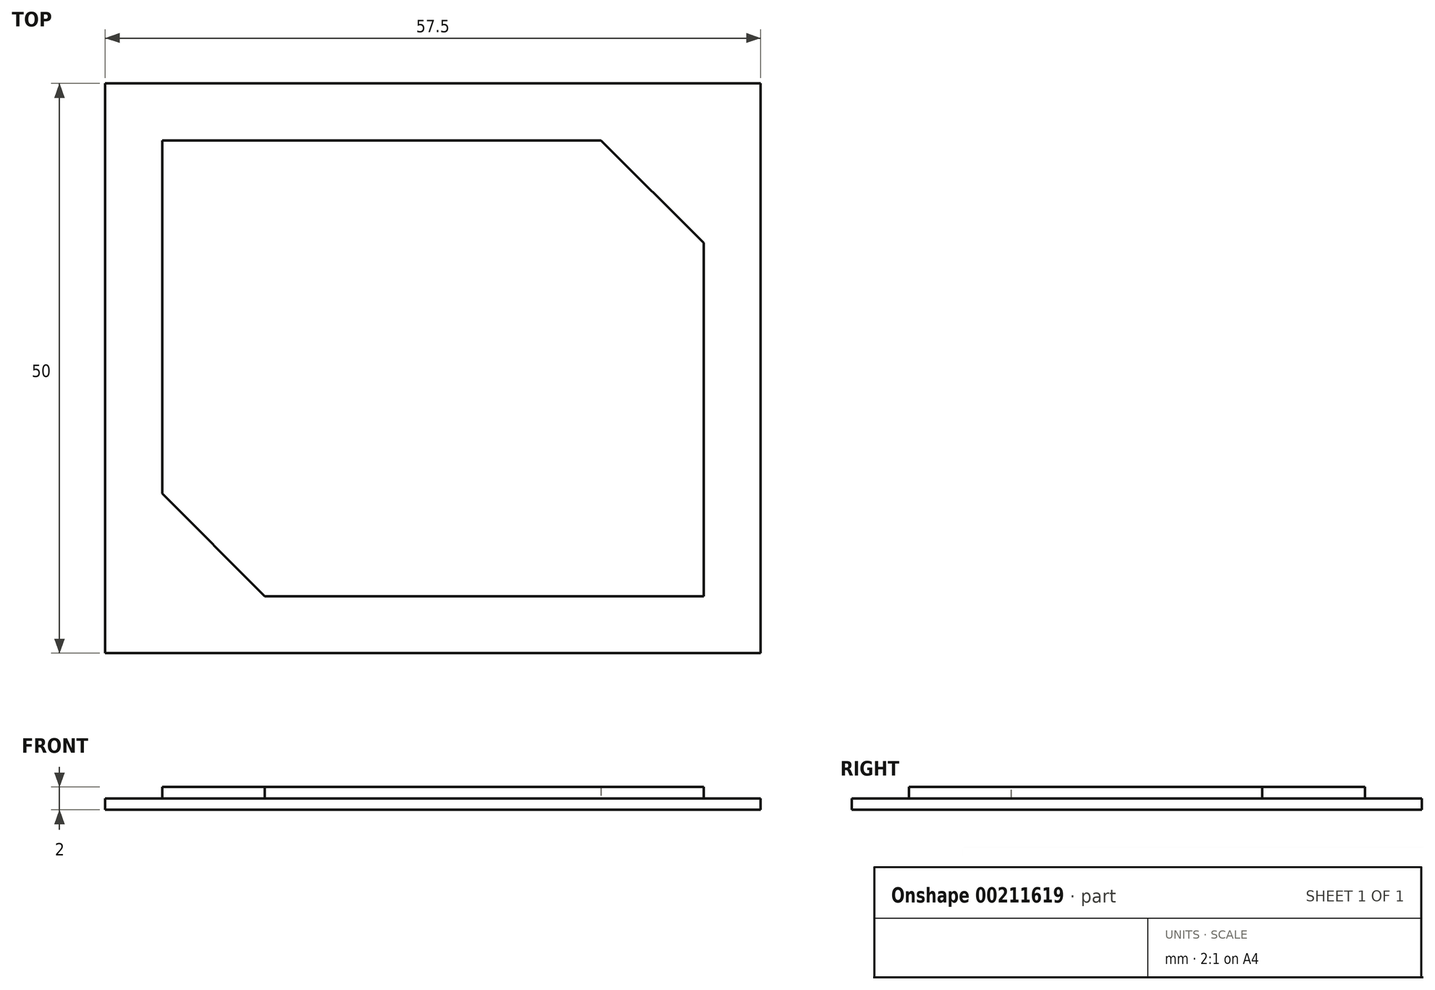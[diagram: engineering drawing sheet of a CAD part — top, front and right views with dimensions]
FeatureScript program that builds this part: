
annotation { "Feature Type Name" : "Feature", "Feature Type Description" : "" }
export const myFeature = defineFeature(function(context is Context, id is Id, definition is map)
    precondition{}
    {
        {
            var Q0;
            Q0=qCreatedBy(makeId("Top.planeOp"),FACE);
            var sketch = newSketch(context, id + "F0", { "sketchPlane" : qUnion([Q0])});
            skLineSegment(sketch, "E0.bottom", {"start": v(23.75, -20) * mm, "end": v(-23.75, -20) * mm});
            skLineSegment(sketch, "E0.top", {"start": v(23.75, 20) * mm, "end": v(-23.75, 20) * mm});
            skLineSegment(sketch, "E0.left", {"start": v(23.75, -20) * mm, "end": v(23.75, 20) * mm});
            skLineSegment(sketch, "E0.right", {"start": v(-23.75, -20) * mm, "end": v(-23.75, 20) * mm});
            skPoint(sketch, "E0.middle", {"position": v(0, 0) * mm});
            skLineSegment(sketch, "E1.0", {"start": v(28.75, -25) * mm, "end": v(-28.75, -25) * mm});
            skLineSegment(sketch, "E1.1", {"start": v(28.75, -25) * mm, "end": v(28.75, 25) * mm});
            skLineSegment(sketch, "E1.2", {"start": v(28.75, 25) * mm, "end": v(-28.75, 25) * mm});
            skLineSegment(sketch, "E1.3", {"start": v(-28.75, -25) * mm, "end": v(-28.75, 25) * mm});
            skSolve(sketch);
        }
        {
            var Q0;
            Q0=makeQuery(id+"F0.imprint","IMPRINT",FACE,{"disambiguationData":[TD([[makeQuery(id+"F0.imprint","IMPRINT",EDGE,{"derivedFrom":sQuery(id+"F0.wireOp",EDGE,"E0.bottom")}),-1.0]])]});
            extrude(context, id + "F1", {"entities" : qUnion([Q0]), "depth" : 2 * mm});
        }
        {
            var Q0;
            Q0=makeQuery(id+"F0.imprint","IMPRINT",FACE,{"disambiguationData":[TD([[makeQuery(id+"F0.imprint","IMPRINT",EDGE,{"derivedFrom":sQuery(id+"F0.wireOp",EDGE,"E0.bottom")}),1.0]])]});
            extrude(context, id + "F2", {"entities" : qUnion([Q0]), "operationType" : NewBodyOperationType.ADD, "depth" : 1 * mm});
        }
        {
            var Q0;
            Q0=makeQuery(id+"F1.opExtrude","SWEPT_EDGE",EDGE,{"disambiguationData":[OSD([sQuery(id+"F0.wireOp",EDGE,"E0.bottom"),sQuery(id+"F0.wireOp",EDGE,"E0.right")])]});
            var Q1;
            Q1=makeQuery(id+"F1.opExtrude","SWEPT_EDGE",EDGE,{"disambiguationData":[OSD([sQuery(id+"F0.wireOp",EDGE,"E0.top"),sQuery(id+"F0.wireOp",EDGE,"E0.left")])]});
            chamfer(context, id + "F3", {"entities" : qUnion([Q0, Q1]), "width" : 9 * mm, "tangentPropagation" : true});
        }
    });
